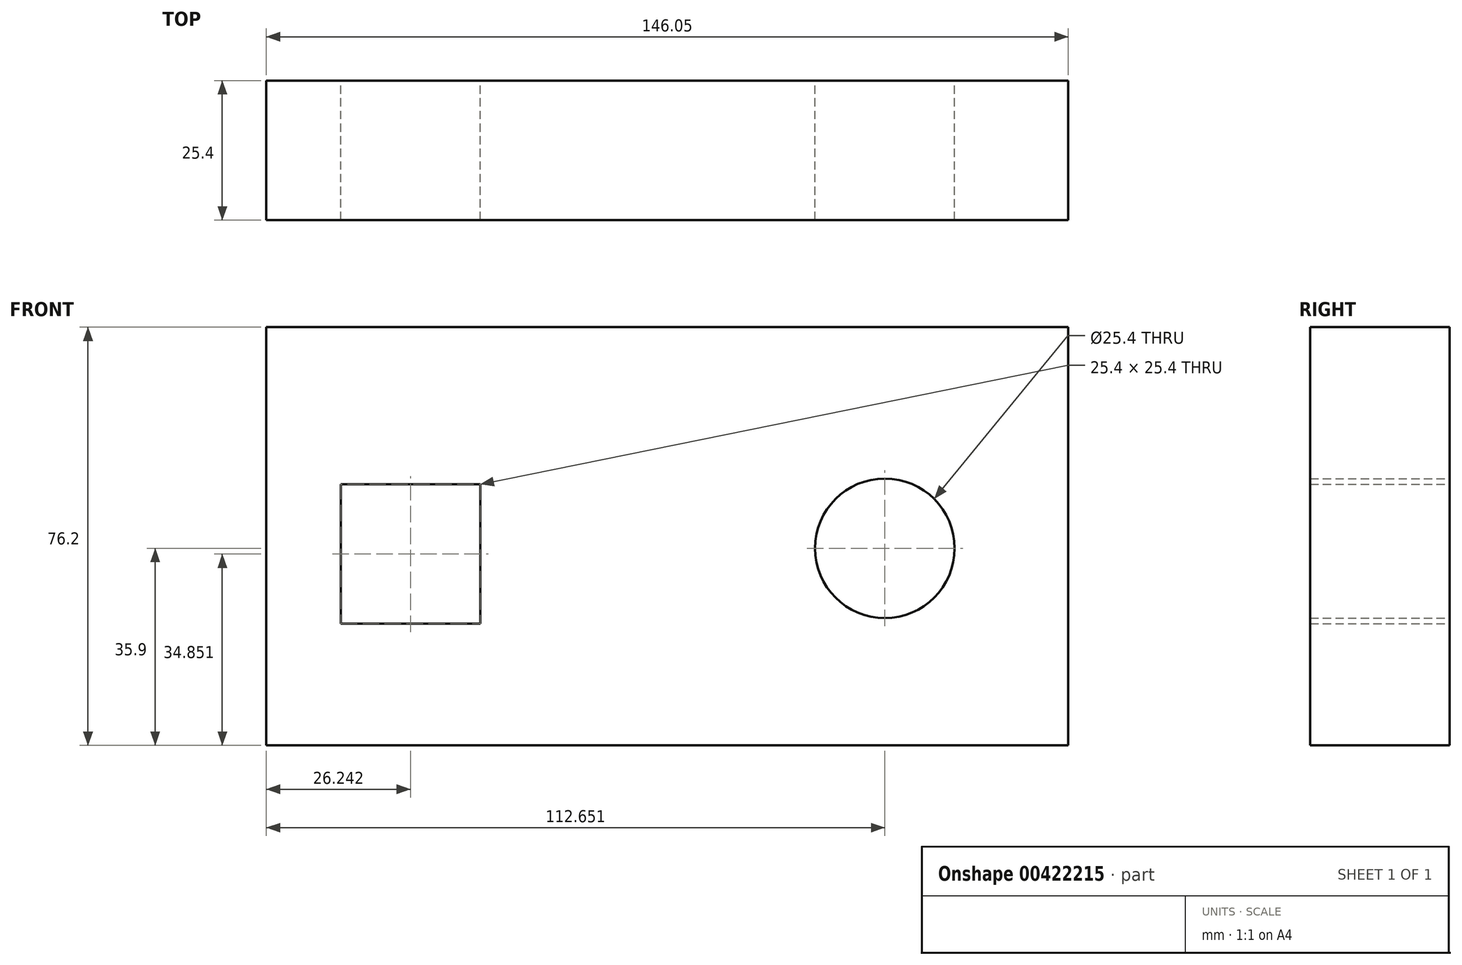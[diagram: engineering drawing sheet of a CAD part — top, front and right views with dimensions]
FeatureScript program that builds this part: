
annotation { "Feature Type Name" : "Feature", "Feature Type Description" : "" }
export const myFeature = defineFeature(function(context is Context, id is Id, definition is map)
    precondition{}
    {
        {
            var Q0;
            Q0=qCreatedBy(makeId("Front.planeOp"),FACE);
            var sketch = newSketch(context, id + "F0", { "sketchPlane" : qUnion([Q0])});
            skLineSegment(sketch, "E0.bottom", {"start": v(-74.44, 40.3) * mm, "end": v(71.6, 40.3) * mm});
            skLineSegment(sketch, "E0.top", {"start": v(-74.44, -35.9) * mm, "end": v(71.6, -35.9) * mm});
            skLineSegment(sketch, "E0.left", {"start": v(-74.44, 40.3) * mm, "end": v(-74.44, -35.9) * mm});
            skLineSegment(sketch, "E0.right", {"start": v(71.6, 40.3) * mm, "end": v(71.6, -35.9) * mm});
            skLineSegment(sketch, "E1.bottom", {"start": v(-60.9, 11.65) * mm, "end": v(-35.5, 11.65) * mm});
            skLineSegment(sketch, "E1.top", {"start": v(-60.9, -13.75) * mm, "end": v(-35.5, -13.75) * mm});
            skLineSegment(sketch, "E1.left", {"start": v(-60.9, 11.65) * mm, "end": v(-60.9, -13.75) * mm});
            skLineSegment(sketch, "E1.right", {"start": v(-35.5, 11.65) * mm, "end": v(-35.5, -13.75) * mm});
            skCircle(sketch, "E2", {"center": v(38.21, 0) * mm, "radius": 12.7 * mm});
            skSolve(sketch);
        }
        {
            var Q0;
            Q0=makeQuery(id+"F0.imprint","IMPRINT",FACE,{"disambiguationData":[TD([[makeQuery(id+"F0.imprint","IMPRINT",EDGE,{"derivedFrom":sQuery(id+"F0.wireOp",EDGE,"E0.bottom")}),-1.0]])]});
            extrude(context, id + "F1", {"entities" : qUnion([Q0]), "depth" : 25.4 * mm});
        }
    });
